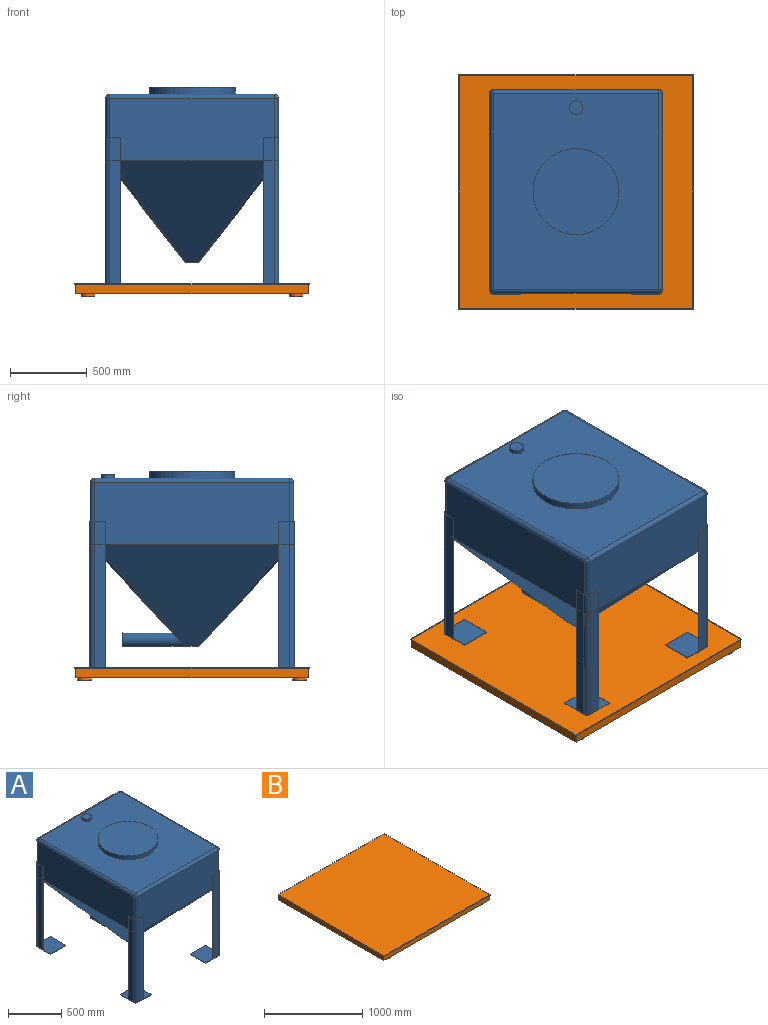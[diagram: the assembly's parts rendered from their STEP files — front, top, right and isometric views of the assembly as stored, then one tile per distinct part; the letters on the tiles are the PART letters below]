
ASSEMBLY  parts=2 mates=1
PART A: 84 faces, bbox 1127.2x1330.4x1276.4 mm
  f0: plane 947.74x4.76mm, normal (-1,0,0), area 4513.6mm2, adj f1,f25,f63,f64,f79
  f1: plane 795.34x71.44mm, normal (0,1,0), area 56816.9mm2, adj f0,f2,f37,f79
  f2: cylinder r=25.4mm len=795.34mm, axis (0,0,-1), area 31732.6mm2, adj f1,f3,f44,f79
  f3: plane 795.34x71.44mm, normal (-1,0,0), area 56816.9mm2, adj f2,f4,f43,f79
  f4: plane 947.74x4.76mm, normal (0,1,0), area 4513.6mm2, adj f3,f20,f61,f64,f79
  f5: plane 947.74x4.76mm, normal (1,0,0), area 4513.6mm2, adj f9,f25,f45,f48,f74
  f6: plane 947.74x4.76mm, normal (0,1,0), area 4513.6mm2, adj f7,f23,f47,f48,f74
  f7: plane 795.34x71.44mm, normal (1,0,0), area 56816.9mm2, adj f6,f8,f39,f74
  f8: cylinder r=25.4mm len=795.34mm, axis (0,0,-1), area 31732.6mm2, adj f7,f9,f38,f74
  f9: plane 795.34x71.44mm, normal (0,1,0), area 56816.9mm2, adj f5,f8,f37,f74
  f10: plane 947.74x4.76mm, normal (0,-1,0), area 4513.6mm2, adj f14,f23,f50,f53,f73
  f11: plane 947.74x4.76mm, normal (1,0,0), area 4513.6mm2, adj f12,f22,f52,f53,f73
  f12: plane 795.34x71.44mm, normal (0,-1,0), area 56816.9mm2, adj f11,f13,f41,f73
  f13: cylinder r=25.4mm len=795.34mm, axis (0,0,-1), area 31732.6mm2, adj f12,f14,f40,f73
  f14: plane 795.34x71.44mm, normal (1,0,0), area 56816.9mm2, adj f10,f13,f39,f73
  f15: plane 947.74x4.76mm, normal (0,-1,0), area 4513.6mm2, adj f16,f20,f57,f59,f70
  f16: plane 795.34x71.44mm, normal (-1,0,0), area 56816.9mm2, adj f15,f43,f58,f70
  f17: plane 795.34x71.44mm, normal (0,-1,0), area 56816.9mm2, adj f18,f41,f58,f70
  f18: plane 947.74x4.76mm, normal (-1,0,0), area 4513.6mm2, adj f17,f22,f55,f59,f70
  f19: cylinder r=25.4mm len=254mm, axis (0,0,1), area 10134.1mm2, adj f20,f25,f35,f64
  f20: plane 1270x406.4mm, normal (1,0,0), area 494353.8mm2, adj f4,f15,f19,f21,f34,f43,f59,f64
  f21: cylinder r=25.4mm len=254mm, axis (0,0,-1), area 10134.1mm2, adj f20,f22,f32,f59
  f22: plane 1066.8x406.4mm, normal (0,1,0), area 411773.4mm2, adj f11,f18,f21,f24,f30,f41,f53,f59
  f23: plane 1270x406.4mm, normal (-1,0,0), area 494353.8mm2, adj f6,f10,f24,f26,f29,f39,f48,f53
  f24: cylinder r=25.4mm len=254mm, axis (0,0,1), area 10134.1mm2, adj f22,f23,f28,f53
  f25: plane 1066.8x406.4mm, normal (0,-1,0), area 411773.4mm2, adj f0,f5,f19,f26,f33,f37,f48,f64
  f26: cylinder r=25.4mm len=254mm, axis (0,0,-1), area 10134.1mm2, adj f23,f25,f31,f48
  f27: plane 1270x1066.8mm, normal (0,0,1), area 1103382.4mm2, adj f29,f30,f33,f34,f80,f82
  f28: sphere r=25.4mm, area 1013.4mm2, adj f24,f29,f30
  f29: cylinder r=25.4mm len=1270mm, axis (0,1,0), area 50670.7mm2, adj f23,f27,f28,f31
  f30: cylinder r=25.4mm len=1066.8mm, axis (1,0,0), area 42563.4mm2, adj f22,f27,f28,f32
  f31: sphere r=25.4mm, area 1013.4mm2, adj f26,f29,f33
  f32: sphere r=25.4mm, area 1013.4mm2, adj f21,f30,f34
  f33: cylinder r=25.4mm len=1066.8mm, axis (-1,0,0), area 42563.4mm2, adj f25,f27,f31,f35
  f34: cylinder r=25.4mm len=1270mm, axis (0,-1,0), area 50670.7mm2, adj f20,f27,f32,f35
  f35: sphere r=25.4mm, area 1013.4mm2, adj f19,f33,f34
  f36: plane 88.99x88.99mm, normal (0,0,-1), area 7897.6mm2, adj f37,f38,f39,f40,f41,f42,f43,f44
  f37: plane 1066.8x660.4mm, normal (0,-0.73,-0.68), area 519541.1mm2, adj f1,f9,f25,f36,f38,f44
  f38: bspline ~1297.26x1093.98mm, area 21361.6mm2, adj f8,f36,f37,f39
  f39: plane 1270x660.4mm, normal (-0.79,0,-0.61), area 566620.2mm2, adj f7,f14,f23,f36,f38,f40
  f40: bspline ~1297.26x1093.98mm, area 21361.6mm2, adj f13,f36,f39,f41
  f41: plane 1066.8x660.4mm, normal (0,0.73,-0.68), area 511053.1mm2, adj f12,f17,f22,f36,f40,f42,f66
  f42: bspline ~1297.26x1093.98mm, area 21361.6mm2, adj f36,f41,f43,f58
  f43: plane 1270x660.4mm, normal (0.79,0,-0.61), area 566620.2mm2, adj f3,f16,f20,f36,f42,f44
  f44: bspline ~1297.26x660.4mm, area 21361.6mm2, adj f2,f36,f37,f43
  f45: plane 952.5x173.04mm, normal (0,-1,0), area 68528.1mm2, adj f5,f46,f48,f49,f74,f76
  f46: cylinder r=30.16mm len=952.5mm, axis (0,0,-1), area 45128.6mm2, adj f45,f47,f48,f49
  f47: plane 952.5x173.04mm, normal (-1,0,0), area 68528.1mm2, adj f6,f46,f48,f49,f74,f75
  f48: plane 101.6x101.6mm, normal (0,0,1), area 888.3mm2, adj f5,f6,f23,f25,f26,f45,f46,f47
  f49: plane 203.2x203.2mm, normal (0,0,-1), area 41095mm2, adj f45,f46,f47,f75,f76
  f50: plane 952.5x173.04mm, normal (-1,0,0), area 68528.1mm2, adj f10,f51,f53,f54,f72,f73
  f51: cylinder r=30.16mm len=952.5mm, axis (0,0,-1), area 45128.6mm2, adj f50,f52,f53,f54
  f52: plane 952.5x173.04mm, normal (0,1,0), area 68528.1mm2, adj f11,f51,f53,f54,f71,f73
  f53: plane 101.6x101.6mm, normal (0,0,1), area 888.3mm2, adj f10,f11,f22,f23,f24,f50,f51,f52
  f54: plane 203.2x203.2mm, normal (0,0,-1), area 41095mm2, adj f50,f51,f52,f71,f72
  f55: plane 952.5x173.04mm, normal (0,1,0), area 68528.1mm2, adj f18,f56,f59,f60,f69,f70
  f56: cylinder r=30.16mm len=952.5mm, axis (0,0,-1), area 45128.6mm2, adj f55,f57,f59,f60
  f57: plane 952.5x173.04mm, normal (1,0,0), area 68528.1mm2, adj f15,f56,f59,f60,f68,f70
  f58: cylinder r=25.4mm len=795.34mm, axis (0,0,-1), area 31732.6mm2, adj f16,f17,f42,f70
  f59: plane 101.6x101.6mm, normal (0,0,1), area 888.3mm2, adj f15,f18,f20,f21,f22,f55,f56,f57
  f60: plane 203.2x203.2mm, normal (0,0,-1), area 41095mm2, adj f55,f56,f57,f68,f69
  f61: plane 952.5x173.04mm, normal (1,0,0), area 68528.1mm2, adj f4,f62,f64,f65,f78,f79
  f62: cylinder r=30.16mm len=952.5mm, axis (0,0,-1), area 45128.6mm2, adj f61,f63,f64,f65
  f63: plane 952.5x173.04mm, normal (0,-1,0), area 68528.1mm2, adj f0,f62,f64,f65,f77,f79
  f64: plane 101.6x101.6mm, normal (0,0,1), area 888.3mm2, adj f0,f4,f19,f20,f25,f61,f62,f63
  f65: plane 203.2x203.2mm, normal (0,0,-1), area 41095mm2, adj f61,f62,f63,f77,f78
  f66: cylinder r=44.45mm len=407.69mm, axis (0,-1,0), area 102278.6mm2, adj f41,f67
  f67: plane 88.9x88.9mm, normal (0,1,0), area 6207.2mm2, adj f66
  f68: plane 203.2x4.76mm, normal (0,-1,0), area 967.7mm2, adj f57,f60,f69,f70
  f69: plane 203.2x4.76mm, normal (-1,0,0), area 967.7mm2, adj f55,f60,f68,f70
  f70: plane 203.2x203.2mm, normal (0,0,1), area 40206.7mm2, adj f15,f16,f17,f18,f55,f57,f58,f68
  f71: plane 203.2x4.76mm, normal (1,0,0), area 967.7mm2, adj f52,f54,f72,f73
  f72: plane 203.2x4.76mm, normal (0,-1,0), area 967.7mm2, adj f50,f54,f71,f73
  f73: plane 203.2x203.2mm, normal (0,0,1), area 40206.7mm2, adj f10,f11,f12,f13,f14,f50,f52,f71
  f74: plane 203.2x203.2mm, normal (0,0,1), area 40206.7mm2, adj f5,f6,f7,f8,f9,f45,f47,f75
  f75: plane 203.2x4.76mm, normal (0,1,0), area 967.7mm2, adj f47,f49,f74,f76
  f76: plane 203.2x4.76mm, normal (1,0,0), area 967.7mm2, adj f45,f49,f74,f75
  f77: plane 203.2x4.76mm, normal (-1,0,0), area 967.7mm2, adj f63,f65,f78,f79
  f78: plane 203.2x4.76mm, normal (0,1,0), area 967.7mm2, adj f61,f65,f77,f79
  f79: plane 203.2x203.2mm, normal (0,0,1), area 40206.7mm2, adj f0,f1,f2,f3,f4,f61,f63,f77
  f80: cylinder r=279.4mm len=558.8mm, axis (0,0,-1), area 78033mm2, adj f27,f81
  f81: plane 558.8x558.8mm, normal (0,0,1), area 245246.4mm2, adj f80
  f82: cylinder r=44.45mm len=88.9mm, axis (0,0,-1), area 7093.9mm2, adj f27,f83
  f83: plane 88.9x88.9mm, normal (0,0,1), area 6207.2mm2, adj f82
PART B: 19 faces, bbox 1524x1524x82.6 mm
  f0: plane 1511.3x58.74mm, normal (0,1,0), area 88770mm2, adj f1,f3,f4,f9
  f1: plane 1511.3x58.74mm, normal (-1,0,0), area 88770mm2, adj f0,f2,f4,f9
  f2: plane 1511.3x58.74mm, normal (0,-1,0), area 88770mm2, adj f1,f3,f4,f9
  f3: plane 1511.3x58.74mm, normal (1,0,0), area 88770mm2, adj f0,f2,f4,f9
  f4: plane 1511.3x1511.3mm, normal (0,0,-1), area 2259198.9mm2, adj f0,f1,f2,f3,f11,f13,f15,f17
  f5: plane 1524x4.76mm, normal (1,0,0), area 7258mm2, adj f6,f8,f9,f10
  f6: plane 1524x4.76mm, normal (0,1,0), area 7258mm2, adj f5,f7,f9,f10
  f7: plane 1524x4.76mm, normal (-1,0,0), area 7258mm2, adj f6,f8,f9,f10
  f8: plane 1524x4.76mm, normal (0,-1,0), area 7258mm2, adj f5,f7,f9,f10
  f9: plane 1524x1524mm, normal (0,0,-1), area 38548.4mm2, adj f0,f1,f2,f3,f5,f6,f7,f8
  f10: plane 1524x1524mm, normal (0,0,1), area 2322576mm2, adj f5,f6,f7,f8
  f11: cylinder r=44.45mm len=88.9mm, axis (0,0,1), area 5320.4mm2, adj f4,f12
  f12: plane 88.9x88.9mm, normal (0,0,-1), area 6207.2mm2, adj f11
  f13: cylinder r=44.45mm len=88.9mm, axis (0,0,1), area 5320.4mm2, adj f4,f14
  f14: plane 88.9x88.9mm, normal (0,0,-1), area 6207.2mm2, adj f13
  f15: cylinder r=44.45mm len=88.9mm, axis (0,0,1), area 5320.4mm2, adj f4,f16
  f16: plane 88.9x88.9mm, normal (0,0,-1), area 6207.2mm2, adj f15
  f17: cylinder r=44.45mm len=88.9mm, axis (0,0,1), area 5320.4mm2, adj f4,f18
  f18: plane 88.9x88.9mm, normal (0,0,-1), area 6207.2mm2, adj f17
PLACE A t=(632.98,1363.1,565.36)mm
PLACE B t=(632.98,1363.1,-234.74)mm
MATE slider A.f80 <-> B.f10  axis (0,0,-1) through (632.98,1363.1,-95.04)mm
